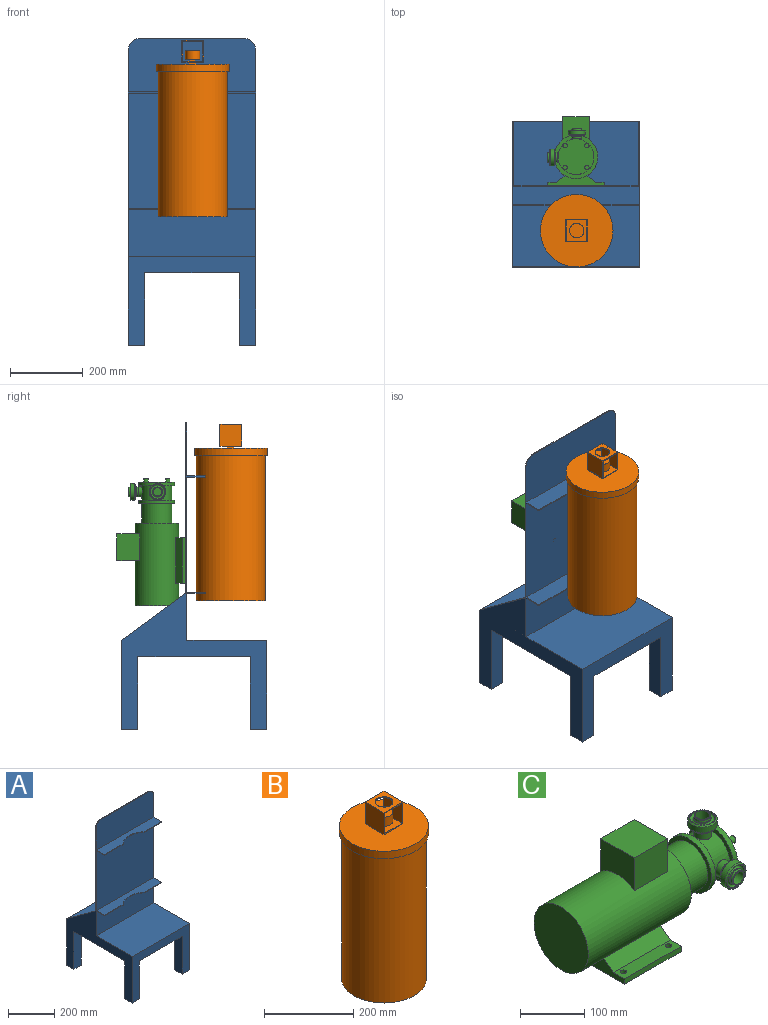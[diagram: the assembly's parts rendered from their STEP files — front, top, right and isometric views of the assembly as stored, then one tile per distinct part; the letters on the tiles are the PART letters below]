
ASSEMBLY  parts=3 mates=2
PART A: 40 faces, bbox 350x400x845 mm
  f0: plane 106.69x3mm, normal (0,-1,0), area 320.1mm2, adj f6,f32,f33,f39
  f1: plane 106.69x3mm, normal (0,-1,0), area 320.1mm2, adj f6,f35,f36,f38
  f2: plane 350x130mm, normal (0,-1,0), area 45500mm2, adj f6,f8,f9,f35
  f3: plane 350x317mm, normal (0,-1,0), area 110950mm2, adj f6,f8,f32,f36
  f4: plane 344x177mm, normal (0,0,1), area 60888mm2, adj f7,f24,f29,f31
  f5: plane 350x245mm, normal (0,-1,0), area 33750mm2, adj f6,f8,f9,f10,f12,f13,f15,f16
  f6: plane 815x400mm, normal (1,0,0), area 49515mm2, adj f0,f1,f2,f3,f5,f7,f9,f10
  f7: plane 350x245mm, normal (0,1,0), area 33750mm2, adj f4,f6,f8,f10,f18,f19,f21,f22
  f8: plane 815x400mm, normal (-1,0,0), area 49515mm2, adj f2,f3,f5,f7,f9,f10,f11,f13
  f9: plane 350x220mm, normal (0,0,1), area 77000mm2, adj f2,f5,f6,f8
  f10: plane 400x350mm, normal (0,0,-1), area 131900mm2, adj f5,f6,f7,f8,f11,f12,f14,f15
  f11: plane 200x45mm, normal (0,1,0), area 9000mm2, adj f8,f10,f12,f13
  f12: plane 200x45mm, normal (1,0,0), area 9000mm2, adj f5,f10,f11,f13
  f13: plane 45x45mm, normal (0,0,-1), area 2025mm2, adj f5,f8,f11,f12
  f14: plane 200x45mm, normal (0,1,0), area 9000mm2, adj f6,f10,f15,f16
  f15: plane 200x45mm, normal (-1,0,0), area 9000mm2, adj f5,f10,f14,f16
  f16: plane 45x45mm, normal (0,0,-1), area 2025mm2, adj f5,f6,f14,f15
  f17: plane 200x45mm, normal (0,-1,0), area 9000mm2, adj f8,f10,f18,f19
  f18: plane 200x45mm, normal (1,0,0), area 9000mm2, adj f7,f10,f17,f19
  f19: plane 45x45mm, normal (0,0,-1), area 2025mm2, adj f7,f8,f17,f18
  f20: plane 200x45mm, normal (0,-1,0), area 9000mm2, adj f6,f10,f21,f22
  f21: plane 200x45mm, normal (-1,0,0), area 9000mm2, adj f7,f10,f20,f22
  f22: plane 45x45mm, normal (0,0,-1), area 2025mm2, adj f6,f7,f20,f21
  f23: plane 350x147mm, normal (0,-1,0), area 51063.7mm2, adj f6,f8,f25,f26,f27,f33
  f24: plane 600x350mm, normal (0,1,0), area 208833.7mm2, adj f4,f6,f8,f25,f26,f27,f28,f29
  f25: plane 290x3mm, normal (0,0,1), area 870mm2, adj f23,f24,f26,f27
  f26: cylinder r=30mm len=30mm, axis (0,-1,0), area 141.4mm2, adj f6,f23,f24,f25
  f27: cylinder r=30mm len=30mm, axis (0,1,0), area 141.4mm2, adj f8,f23,f24,f25
  f28: plane 177x130mm, normal (0,0.59,0.81), area 658.8mm2, adj f6,f7,f24,f29
  f29: plane 177x130mm, normal (-1,0,0), area 11505mm2, adj f4,f24,f28
  f30: plane 177x130mm, normal (0,0.59,0.81), area 658.8mm2, adj f7,f8,f24,f31
  f31: plane 177x130mm, normal (1,0,0), area 11505mm2, adj f4,f24,f30
  f32: plane 350x50mm, normal (0,0,-1), area 15295.6mm2, adj f0,f3,f6,f8,f34,f39
  f33: plane 350x50mm, normal (0,0,1), area 15295.6mm2, adj f0,f6,f8,f23,f34,f39
  f34: plane 114.86x3mm, normal (0,-1,0), area 344.6mm2, adj f8,f32,f33,f39
  f35: plane 350x50mm, normal (0,0,-1), area 15295.6mm2, adj f1,f2,f6,f8,f37,f38
  f36: plane 350x50mm, normal (0,0,1), area 15295.6mm2, adj f1,f3,f6,f8,f37,f38
  f37: plane 114.86x3mm, normal (0,-1,0), area 344.6mm2, adj f8,f35,f36,f38
  f38: cylinder r=95mm len=128.45mm, axis (0,0,1), area 423.2mm2, adj f1,f35,f36,f37
  f39: cylinder r=95mm len=128.45mm, axis (0,0,1), area 423.2mm2, adj f0,f32,f33,f34
PART B: 27 faces, bbox 200x200x485 mm
  f0: plane 200x200mm, normal (0,0,1), area 31015.9mm2, adj f3,f5,f6,f7,f8
  f1: cylinder r=95mm len=400mm, axis (0,0,-1), area 238761mm2, adj f2,f4
  f2: plane 190x190mm, normal (0,0,-1), area 28352.9mm2, adj f1
  f3: cylinder r=100mm len=200mm, axis (0,0,-1), area 12566.4mm2, adj f0,f4
  f4: plane 200x200mm, normal (0,0,-1), area 3063.1mm2, adj f1,f3
  f5: plane 20x5mm, normal (0,-1,0), area 100mm2, adj f0,f6,f8,f14
  f6: plane 20x5mm, normal (1,0,0), area 100mm2, adj f0,f5,f7,f14
  f7: plane 20x5mm, normal (0,1,0), area 100mm2, adj f0,f6,f8,f14
  f8: plane 20x5mm, normal (-1,0,0), area 100mm2, adj f0,f5,f7,f14
  f9: plane 60x60mm, normal (0,-1,0), area 575mm2, adj f10,f12,f13,f14,f15,f16,f17,f18
  f10: plane 60x60mm, normal (1,0,0), area 3600mm2, adj f9,f11,f13,f14
  f11: plane 60x60mm, normal (0,1,0), area 575mm2, adj f10,f12,f13,f14,f15,f16,f17,f18
  f12: plane 60x60mm, normal (-1,0,0), area 3600mm2, adj f9,f11,f13,f14
  f13: plane 60x60mm, normal (0,0,1), area 2343.4mm2, adj f9,f10,f11,f12,f19
  f14: plane 60x60mm, normal (0,0,-1), area 3200mm2, adj f5,f6,f7,f8,f9,f10,f11,f12
  f15: plane 60x55mm, normal (0,0,-1), area 2043.4mm2, adj f9,f11,f16,f18,f19
  f16: plane 60x55mm, normal (1,0,0), area 3300mm2, adj f9,f11,f15,f17
  f17: plane 60x55mm, normal (0,0,1), area 3075mm2, adj f9,f11,f16,f18,f20,f21,f22,f23
  f18: plane 60x55mm, normal (-1,0,0), area 3300mm2, adj f9,f11,f15,f17
  f19: cylinder r=20mm len=40mm, axis (0,0,1), area 314.2mm2, adj f13,f15
  f20: plane 15x5mm, normal (0,-1,0), area 75mm2, adj f17,f21,f23,f26
  f21: plane 15x5mm, normal (1,0,0), area 75mm2, adj f17,f20,f22,f26
  f22: plane 15x5mm, normal (0,1,0), area 75mm2, adj f17,f21,f23,f26
  f23: plane 15x5mm, normal (-1,0,0), area 75mm2, adj f17,f20,f22,f26
  f24: cylinder r=20mm len=40mm, axis (0,0,-1), area 3141.6mm2, adj f25,f26
  f25: plane 40x40mm, normal (0,0,1), area 1256.6mm2, adj f24
  f26: plane 40x40mm, normal (0,0,-1), area 1031.6mm2, adj f20,f21,f22,f23,f24
PART C: 71 faces, bbox 350x155.5x190 mm
  f0: cone r=23mm half-angle=45deg, axis (0,-1,0), area 391mm2, adj f1,f13
  f1: cylinder r=23mm len=46mm, axis (0,1,0), area 1546.3mm2, adj f0,f2
  f2: cone r=21mm half-angle=45deg, axis (0,1,0), area 391mm2, adj f1,f12
  f3: cylinder r=19.8mm len=39.6mm, axis (0,1,0), area 199.1mm2, adj f4,f12
  f4: torus R=16.62mm, axis (0,-1,0), area 1041.9mm2, adj f3,f5
  f5: cylinder r=13.45mm len=26.9mm, axis (0,1,0), area 135.2mm2, adj f4,f6
  f6: cone r=12.86mm half-angle=8.5deg, axis (0,1,0), area 329.9mm2, adj f5,f7
  f7: torus R=11.87mm, axis (0,-1,0), area 111.5mm2, adj f6,f11
  f8: cylinder r=11.45mm len=26.5mm, axis (0,1,0), area 1906.5mm2, adj f11,f52
  f9: cylinder r=13.25mm len=26.5mm, axis (0,1,0), area 374.6mm2, adj f10,f14
  f10: torus R=15.75mm, axis (0,-1,0), area 349.3mm2, adj f9,f13
  f11: plane 23.74x23.74mm, normal (0,-1,0), area 30.8mm2, adj f7,f8
  f12: plane 42x42mm, normal (0,-1,0), area 153.8mm2, adj f2,f3
  f13: plane 42x42mm, normal (0,1,0), area 606.1mm2, adj f0,f10
  f14: plane 28x28mm, normal (0,-1,0), area 64.2mm2, adj f9,f38
  f15: cone r=23mm half-angle=45deg, axis (0,0,1), area 391mm2, adj f16,f28
  f16: cylinder r=23mm len=46mm, axis (0,0,-1), area 1546.3mm2, adj f15,f17
  f17: cone r=21mm half-angle=45deg, axis (0,0,-1), area 391mm2, adj f16,f27
  f18: cylinder r=19.8mm len=39.6mm, axis (0,0,-1), area 199.1mm2, adj f19,f27
  f19: torus R=16.62mm, axis (0,0,1), area 1041.9mm2, adj f18,f20
  f20: cylinder r=13.45mm len=26.9mm, axis (0,0,-1), area 135.2mm2, adj f19,f21
  f21: cone r=12.86mm half-angle=8.5deg, axis (0,0,-1), area 329.9mm2, adj f20,f22
  f22: torus R=11.87mm, axis (0,0,1), area 111.5mm2, adj f21,f26
  f23: cylinder r=11.45mm len=26.5mm, axis (0,0,-1), area 1906.5mm2, adj f26,f51
  f24: cylinder r=13.25mm len=26.5mm, axis (0,0,-1), area 374.6mm2, adj f25,f29
  f25: torus R=15.75mm, axis (0,0,1), area 349.3mm2, adj f24,f28
  f26: plane 23.74x23.74mm, normal (0,0,1), area 30.8mm2, adj f22,f23
  f27: plane 42x42mm, normal (0,0,1), area 153.8mm2, adj f17,f18
  f28: plane 42x42mm, normal (0,0,-1), area 606.1mm2, adj f15,f25
  f29: plane 28x28mm, normal (0,0,1), area 64.2mm2, adj f24,f39
  f30: cylinder r=5mm len=10mm, axis (0,0,-1), area 314.2mm2, adj f61,f63
  f31: cylinder r=5mm len=10mm, axis (0,0,-1), area 314.2mm2, adj f61,f63
  f32: cylinder r=5mm len=10mm, axis (0,0,-1), area 314.2mm2, adj f63,f65
  f33: cylinder r=5mm len=10mm, axis (0,0,-1), area 314.2mm2, adj f63,f65
  f34: cylinder r=6mm len=12mm, axis (1,0,0), area 377mm2, adj f45,f56
  f35: cylinder r=6mm len=12mm, axis (1,0,0), area 377mm2, adj f45,f55
  f36: cylinder r=6mm len=12mm, axis (1,0,0), area 377mm2, adj f45,f54
  f37: cylinder r=6mm len=12mm, axis (1,0,0), area 377mm2, adj f45,f53
  f38: cylinder r=14mm len=28mm, axis (0,-1,0), area 990.3mm2, adj f14,f43
  f39: cylinder r=14mm len=28mm, axis (0,0,1), area 988.7mm2, adj f29,f43
  f40: cylinder r=49.5mm len=99mm, axis (1,0,0), area 2799.2mm2, adj f45,f50
  f41: cylinder r=49.5mm len=99mm, axis (1,0,0), area 2799.2mm2, adj f48,f49
  f42: cylinder r=41.5mm len=83mm, axis (1,0,0), area 14341.4mm2, adj f47,f48
  f43: cylinder r=41.5mm len=83mm, axis (1,0,0), area 9039mm2, adj f38,f39,f49,f50
  f44: cylinder r=60mm len=227.5mm, axis (1,0,0), area 72063.2mm2, adj f46,f47,f57,f58,f59,f60,f66,f67
  f45: plane 99x99mm, normal (1,0,0), area 7245.3mm2, adj f34,f35,f36,f37,f40
  f46: plane 120x120mm, normal (-1,0,0), area 11309.7mm2, adj f44
  f47: plane 120x120mm, normal (1,0,0), area 5899.1mm2, adj f42,f44
  f48: plane 99x99mm, normal (-1,0,0), area 2287.1mm2, adj f41,f42
  f49: plane 99x99mm, normal (1,0,0), area 2287.1mm2, adj f41,f43
  f50: plane 99x99mm, normal (-1,0,0), area 2287.1mm2, adj f40,f43
  f51: plane 22.9x22.9mm, normal (0,0,1), area 411.9mm2, adj f23
  f52: plane 22.9x22.9mm, normal (0,-1,0), area 411.9mm2, adj f8
  f53: plane 12x12mm, normal (1,0,0), area 113.1mm2, adj f37
  f54: plane 12x12mm, normal (1,0,0), area 113.1mm2, adj f36
  f55: plane 12x12mm, normal (1,0,0), area 113.1mm2, adj f35
  f56: plane 12x12mm, normal (1,0,0), area 113.1mm2, adj f34
  f57: plane 125x23.06mm, normal (0,0.62,0.79), area 3662.3mm2, adj f44,f59,f60,f61
  f58: plane 125x23.06mm, normal (0,-0.62,0.79), area 3662.3mm2, adj f44,f59,f60,f65
  f59: plane 155x28.07mm, normal (-1,0,0), area 2724.8mm2, adj f44,f57,f58,f61,f62,f63,f64,f65
  f60: plane 155x28.07mm, normal (1,0,0), area 2724.8mm2, adj f44,f57,f58,f61,f62,f63,f64,f65
  f61: plane 125x24.39mm, normal (0,0,1), area 2891.1mm2, adj f30,f31,f57,f59,f60,f62
  f62: plane 125x10mm, normal (0,1,0), area 1250mm2, adj f59,f60,f61,f63
  f63: plane 155x125mm, normal (0,0,-1), area 19060.8mm2, adj f30,f31,f32,f33,f59,f60,f62,f64
  f64: plane 125x10mm, normal (0,-1,0), area 1250mm2, adj f59,f60,f63,f65
  f65: plane 125x24.39mm, normal (0,0,1), area 2891.1mm2, adj f32,f33,f58,f59,f60,f64
  f66: plane 73.61x62.62mm, normal (-1,0,0), area 3975.8mm2, adj f44,f67,f69,f70
  f67: plane 73.61x62.62mm, normal (0,-1,0), area 4609.1mm2, adj f44,f66,f68,f70
  f68: plane 73.61x62.62mm, normal (1,0,0), area 3975.8mm2, adj f44,f67,f69,f70
  f69: plane 73.61x62.62mm, normal (0,1,0), area 4609.1mm2, adj f44,f66,f68,f70
  f70: plane 73.61x73.61mm, normal (0,0,1), area 5418.6mm2, adj f66,f67,f68,f69
PLACE A t=(-358.93,61.62,-94.23)mm
PLACE B t=(-356.93,-39.38,60.77)mm
PLACE C rot(axis=(-0.58,-0.58,-0.58),120deg) t=(-358.93,164.62,46.11)mm
MATE slider B.f1 <-> A.f9  axis (0,0,-1) through (-356.93,-39.38,60.77)mm
MATE planar C.f63 <-> A.f24  axis (0,-1,0) through (-358.93,84.62,171.11)mm
